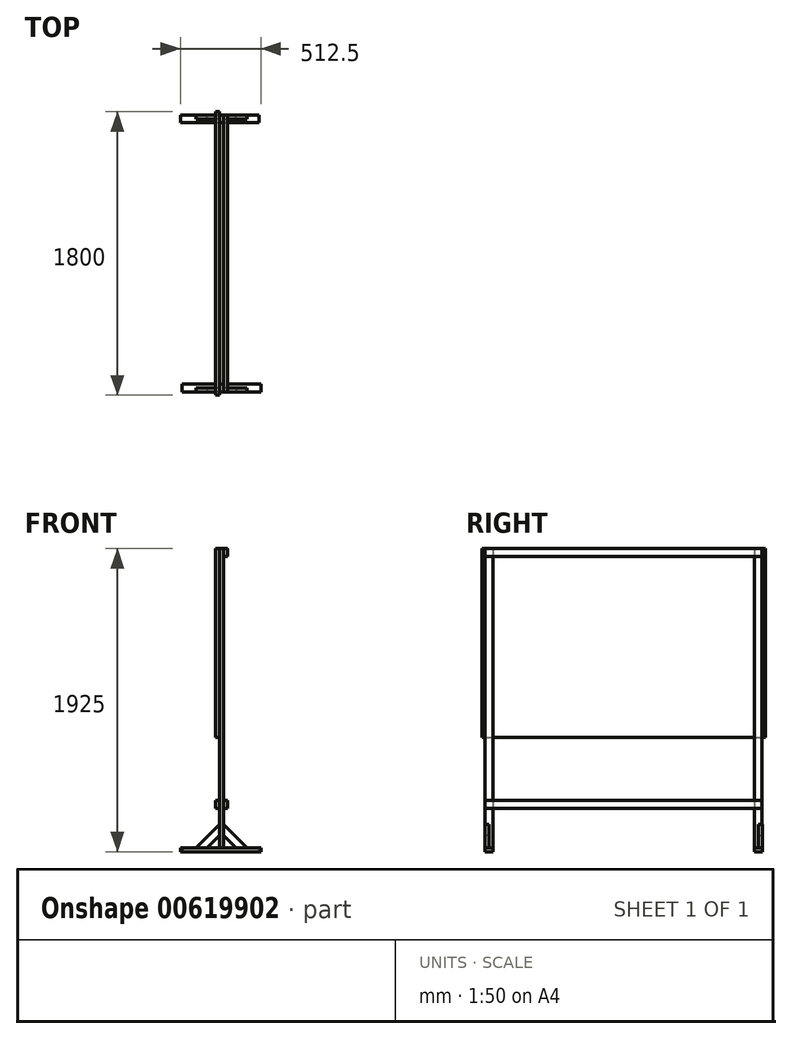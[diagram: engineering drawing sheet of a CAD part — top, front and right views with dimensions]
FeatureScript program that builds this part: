
annotation { "Feature Type Name" : "Feature", "Feature Type Description" : "" }
export const myFeature = defineFeature(function(context is Context, id is Id, definition is map)
    precondition{}
    {
        {
            var Q0;
            Q0=qCreatedBy(makeId("Right.planeOp"),FACE);
            var sketch = newSketch(context, id + "F0", { "sketchPlane" : qUnion([Q0])});
            skLineSegment(sketch, "E0.bottom", {"start": v(-900, 600) * mm, "end": v(900, 600) * mm});
            skLineSegment(sketch, "E0.top", {"start": v(-900, -600) * mm, "end": v(900, -600) * mm});
            skLineSegment(sketch, "E0.left", {"start": v(-900, 600) * mm, "end": v(-900, -600) * mm});
            skLineSegment(sketch, "E0.right", {"start": v(900, 600) * mm, "end": v(900, -600) * mm});
            skPoint(sketch, "E0.middle", {"position": v(0, 0) * mm});
            skSolve(sketch);
        }
        {
            var Q0;
            Q0 = qSketchRegion(id + "F0", true);
            extrude(context, id + "F1", {"entities" : qUnion([Q0]), "depth" : 25 * mm, "offsetDistance" : 25 * mm});
        }
        {
            var Q0;
            Q0=makeQuery(id+"F1.opExtrude","CAP_FACE",FACE,{"disambiguationData":[OSD([sQuery(id+"F0.wireOp",EDGE,"E0.bottom"),sQuery(id+"F0.wireOp",EDGE,"E0.top"),sQuery(id+"F0.wireOp",EDGE,"E0.left"),sQuery(id+"F0.wireOp",EDGE,"E0.right")])],"isStart":false});
            var sketch = newSketch(context, id + "F2", { "sketchPlane" : qUnion([Q0])});
            skLineSegment(sketch, "E1", {"start": v(-1291.29, 620) * mm, "end": v(-1291.29, -1380) * mm});
            skLineSegment(sketch, "E2", {"start": v(-1291.29, -1380) * mm, "end": v(1618.6, -1380) * mm});
            skSolve(sketch);
        }
        {
            var Q0;
            Q0=makeQuery(id+"F2.imprint","IMPRINT",FACE,{"disambiguationData":[TD([[makeQuery(id+"F2.imprint","IMPRINT",EDGE,{"derivedFrom":makeQuery(id+"F1.opExtrude","CAP_EDGE",EDGE,{"disambiguationData":[OSD([sQuery(id+"F0.wireOp",EDGE,"E0.bottom")])],"isStart":false})}),-1.0]])]});
            var sketch = newSketch(context, id + "F3", { "sketchPlane" : qUnion([Q0])});
            skLineSegment(sketch, "E3.bottom", {"start": v(-880, 600) * mm, "end": v(-830, 600) * mm});
            skLineSegment(sketch, "E3.top", {"start": v(-880, -1300) * mm, "end": v(-830, -1300) * mm});
            skLineSegment(sketch, "E3.left", {"start": v(-880, 600) * mm, "end": v(-880, -1300) * mm});
            skLineSegment(sketch, "E3.right", {"start": v(-830, 600) * mm, "end": v(-830, -1300) * mm});
            skLineSegment(sketch, "E4.bottom", {"start": v(830, 600) * mm, "end": v(880, 600) * mm});
            skLineSegment(sketch, "E4.top", {"start": v(830, -1300) * mm, "end": v(880, -1300) * mm});
            skLineSegment(sketch, "E4.left", {"start": v(830, 600) * mm, "end": v(830, -1300) * mm});
            skLineSegment(sketch, "E4.right", {"start": v(880, 600) * mm, "end": v(880, -1300) * mm});
            skSolve(sketch);
        }
        {
            var Q0;
            Q0 = qSketchRegion(id + "F3", true);
            extrude(context, id + "F4", {"entities" : qUnion([Q0]), "depth" : 25 * mm, "offsetDistance" : 25 * mm});
        }
        {
            var Q0;
            Q0=makeQuery(id+"F4.opExtrude","CAP_FACE",FACE,{"disambiguationData":[OSD([sQuery(id+"F3.wireOp",EDGE,"E3.bottom"),sQuery(id+"F3.wireOp",EDGE,"E3.top"),sQuery(id+"F3.wireOp",EDGE,"E3.left"),sQuery(id+"F3.wireOp",EDGE,"E3.right")])],"isStart":false});
            var sketch = newSketch(context, id + "F5", { "sketchPlane" : qUnion([Q0])});
            skLineSegment(sketch, "E5.bottom", {"start": v(-880, -1050) * mm, "end": v(880, -1050) * mm});
            skLineSegment(sketch, "E5.top", {"start": v(-880, -1000) * mm, "end": v(880, -1000) * mm});
            skLineSegment(sketch, "E5.left", {"start": v(-880, -1050) * mm, "end": v(-880, -1000) * mm});
            skLineSegment(sketch, "E5.right", {"start": v(880, -1050) * mm, "end": v(880, -1000) * mm});
            skSolve(sketch);
        }
        {
            var Q0;
            Q0 = qSketchRegion(id + "F5", true);
            extrude(context, id + "F6", {"entities" : qUnion([Q0]), "depth" : 25 * mm, "offsetDistance" : 25 * mm});
        }
        {
            var Q0;
            Q0=makeQuery(id+"F4.opExtrude","CAP_FACE",FACE,{"disambiguationData":[OSD([sQuery(id+"F3.wireOp",EDGE,"E4.bottom"),sQuery(id+"F3.wireOp",EDGE,"E4.top"),sQuery(id+"F3.wireOp",EDGE,"E4.left"),sQuery(id+"F3.wireOp",EDGE,"E4.right")])],"isStart":true});
            var sketch = newSketch(context, id + "F7", { "sketchPlane" : qUnion([Q0])});
            skLineSegment(sketch, "E6.bottom", {"start": v(-880, -1050) * mm, "end": v(880, -1050) * mm});
            skLineSegment(sketch, "E6.top", {"start": v(-880, -1000) * mm, "end": v(880, -1000) * mm});
            skLineSegment(sketch, "E6.left", {"start": v(-880, -1050) * mm, "end": v(-880, -1000) * mm});
            skLineSegment(sketch, "E6.right", {"start": v(880, -1050) * mm, "end": v(880, -1000) * mm});
            skSolve(sketch);
        }
        {
            var Q0;
            Q0 = qSketchRegion(id + "F7", true);
            extrude(context, id + "F8", {"entities" : qUnion([Q0]), "depth" : 25 * mm, "offsetDistance" : 25 * mm});
        }
        {
            var Q0;
            Q0=makeQuery(id+"F4.opExtrude","SWEPT_FACE",FACE,{"disambiguationData":[OSD([sQuery(id+"F3.wireOp",EDGE,"E3.top")])]});
            var sketch = newSketch(context, id + "F9", { "sketchPlane" : qUnion([Q0])});
            skPoint(sketch, "E7.firstSnap0", {"position": v(37.5, 880) * mm});
            skLineSegment(sketch, "E7.bottom", {"start": v(287.5, 880) * mm, "end": v(-212.5, 880) * mm});
            skLineSegment(sketch, "E7.top", {"start": v(287.5, 830) * mm, "end": v(-212.5, 830) * mm});
            skLineSegment(sketch, "E7.left", {"start": v(287.5, 880) * mm, "end": v(287.5, 830) * mm});
            skLineSegment(sketch, "E7.right", {"start": v(-212.5, 880) * mm, "end": v(-212.5, 830) * mm});
            skLineSegment(sketch, "E8.bottom", {"start": v(-225, -880.2) * mm, "end": v(275, -880.2) * mm});
            skLineSegment(sketch, "E8.top", {"start": v(-225, -830.2) * mm, "end": v(275, -830.2) * mm});
            skLineSegment(sketch, "E8.left", {"start": v(-225, -880.2) * mm, "end": v(-225, -830.2) * mm});
            skLineSegment(sketch, "E8.right", {"start": v(275, -880.2) * mm, "end": v(275, -830.2) * mm});
            skSolve(sketch);
        }
        {
            var Q0;
            Q0 = qSketchRegion(id + "F9", true);
            extrude(context, id + "F10", {"entities" : qUnion([Q0]), "depth" : 25 * mm, "offsetDistance" : 25 * mm});
        }
        {
            var Q0;
            Q0=makeQuery(id+"F4.opExtrude","SWEPT_FACE",FACE,{"disambiguationData":[OSD([sQuery(id+"F3.wireOp",EDGE,"E3.left")])]});
            var sketch = newSketch(context, id + "F11", { "sketchPlane" : qUnion([Q0])});
            skLineSegment(sketch, "E9", {"start": v(25, -1220.71) * mm, "end": v(25, -1150) * mm});
            skLineSegment(sketch, "E10", {"start": v(25, -1150) * mm, "end": v(-125, -1300) * mm});
            skLineSegment(sketch, "E11", {"start": v(-125, -1300) * mm, "end": v(-54.29, -1300) * mm});
            skLineSegment(sketch, "E12", {"start": v(50, -1150) * mm, "end": v(50, -1220.71) * mm});
            skLineSegment(sketch, "E13", {"start": v(129.29, -1300) * mm, "end": v(200, -1300) * mm});
            skLineSegment(sketch, "E14", {"start": v(200, -1300) * mm, "end": v(50, -1150) * mm});
            skLineSegment(sketch, "E15.0", {"start": v(129.29, -1300) * mm, "end": v(50, -1220.71) * mm});
            skLineSegment(sketch, "E16.trimOffspring", {"start": v(25, -1220.71) * mm, "end": v(-54.29, -1300) * mm});
            skSolve(sketch);
        }
        {
            var Q0;
            Q0 = qSketchRegion(id + "F11", true);
            extrude(context, id + "F12", {"entities" : qUnion([Q0]), "oppositeDirection" : true, "depth" : 25 * mm, "offsetDistance" : 25 * mm});
        }
        {
            var Q0;
            Q0=makeQuery(id+"F10.opExtrude","SWEPT_FACE",FACE,{"disambiguationData":[OSD([sQuery(id+"F9.wireOp",EDGE,"E8.bottom")])]});
            var sketch = newSketch(context, id + "F13", { "sketchPlane" : qUnion([Q0])});
            skLineSegment(sketch, "E17", {"start": v(-50, -1220.71) * mm, "end": v(-50, -1150) * mm});
            skLineSegment(sketch, "E18", {"start": v(-50, -1150) * mm, "end": v(-200, -1300) * mm});
            skLineSegment(sketch, "E19", {"start": v(-200, -1300) * mm, "end": v(-129.29, -1300) * mm});
            skLineSegment(sketch, "E20", {"start": v(-25, -1220.71) * mm, "end": v(-25, -1150) * mm});
            skLineSegment(sketch, "E21", {"start": v(-25, -1150) * mm, "end": v(125, -1300) * mm});
            skLineSegment(sketch, "E22", {"start": v(125, -1300) * mm, "end": v(54.29, -1300) * mm});
            skLineSegment(sketch, "E23.trimOffspring", {"start": v(-50, -1220.71) * mm, "end": v(-129.29, -1300) * mm});
            skLineSegment(sketch, "E24.trimOffspring", {"start": v(-25, -1220.71) * mm, "end": v(54.29, -1300) * mm});
            skSolve(sketch);
        }
        {
            var Q0;
            Q0 = qSketchRegion(id + "F13", true);
            extrude(context, id + "F14", {"entities" : qUnion([Q0]), "oppositeDirection" : true, "depth" : 25 * mm, "offsetDistance" : 25 * mm});
        }
        {
            var Q0;
            Q0=makeQuery(id+"F6.opExtrude","SWEPT_BODY",BODY,{"disambiguationData":[OSD([sQuery(id+"F5.wireOp",EDGE,"E5.bottom"),sQuery(id+"F5.wireOp",EDGE,"E5.top"),sQuery(id+"F5.wireOp",EDGE,"E5.left"),sQuery(id+"F5.wireOp",EDGE,"E5.right")])]});
            transform(context, id + "F15", {"entities" : qUnion([Q0]), "transformType" : TransformType.TRANSLATION_3D, "dx" : 0 * mm, "dy" : 0 * mm, "dz" : 1600 * mm, "makeCopy" : true});
        }
    });
